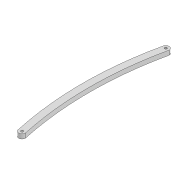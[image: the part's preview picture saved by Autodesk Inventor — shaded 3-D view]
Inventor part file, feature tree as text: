
AUTODESK INVENTOR PART (.ipt)
format: ipt  version: 2022 (Build 260153000, 153)  size: 92,672 bytes
history: native  units: mm
features: extrude x1, sketch x1
ambient origin geometry x8: Origin, YZ Plane, XZ Plane, XY Plane, X Axis, Y Axis, Z Axis, Center Point
bodies: Solid1 (feature_tree)
feature tree (2):
  extrude  "Extrusion1"  Depth=300.0mm
  sketch  "Sketch1"  dims[d0=2.2mm d1=2.2mm d2=6.0mm d3=128.523mm d6=4.0mm d7=0.0mm d14=300.0mm d15=300.0mm]
